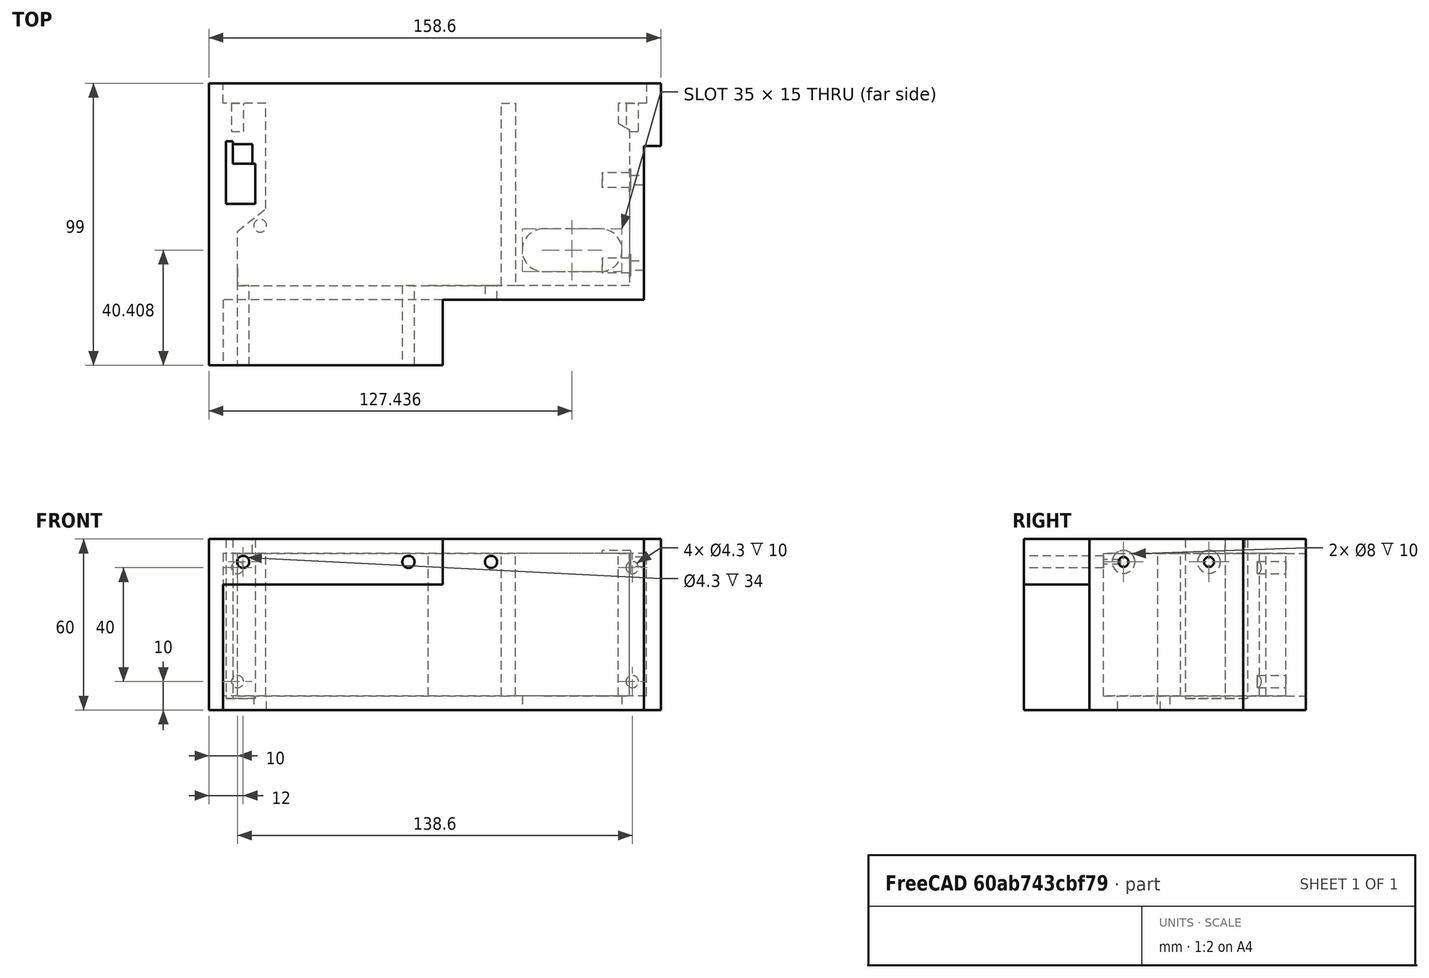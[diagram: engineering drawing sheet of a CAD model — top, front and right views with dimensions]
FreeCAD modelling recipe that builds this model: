
FCSTD DOCUMENT  (FreeCAD 0.21R33668 +7 (Git))
Label: speakerbox-L
License: All rights reserved
LicenseURL: http://en.wikipedia.org/wiki/All_rights_reserved
objects: Sketcher::SketchObject×10, PartDesign::Pocket×9, PartDesign::Plane×4, PartDesign::Pad×1, PartDesign::CoordinateSystem×1, PartDesign::Body×1, App::Part×1
note: 36 computed .brp shape members not serialized (recipe doc carries the construction recipe); baked Part::Feature solids carry a one-line shape summary decoded from their .brp
EXTERNAL_REF file=planB.FCStd obj=Spreadsheet

FEATURE [Sketcher::SketchObject] Sketch
  FullyConstrained = true
  MapMode = 5
  Support = -> [XY_Plane]
  expr: Constraints[13] = planB#<<data>>.central_h + planB#<<data>>.mungo_d + 2
  sketch-geometry (8):
    g0: LineSegment StartX=0 StartY=0 StartZ=0 EndX=82 EndY=0 EndZ=0
    g1: LineSegment StartX=158.6 StartY=99 StartZ=0 EndX=0 EndY=99 EndZ=0
    g2: LineSegment StartX=0 StartY=99 StartZ=0 EndX=0 EndY=0 EndZ=0
    g3: LineSegment StartX=82 StartY=0 StartZ=0 EndX=82 EndY=23 EndZ=0
    g4: LineSegment StartX=82 StartY=23 StartZ=0 EndX=152.6 EndY=23 EndZ=0
    g5: LineSegment StartX=152.6 StartY=23 StartZ=0 EndX=152.6 EndY=77 EndZ=0
    g6: LineSegment StartX=152.6 StartY=77 StartZ=0 EndX=158.6 EndY=77 EndZ=0
    g7: LineSegment StartX=158.6 StartY=77 StartZ=0 EndX=158.6 EndY=99 EndZ=0
  constraints (23):
    c: Coincident(g0,g3)
    c: Coincident(g7,g1)
    c: Coincident(g1,g2)
    c: Coincident(g2,g0)
    c: Horizontal(g0)
    c: Horizontal(g1)
    c: Vertical(g2)
    c: Coincident(g0,g-1)
    c: Coincident(g3,g4)
    c: Vertical(g3)
    c: Coincident(g4,g5)
    c: Horizontal(g4)
    c: Distance(g3) = 23
    c: Distance(g0) = 82
    c: DistanceX(g4) = 152.6
    c: Coincident(g5,g6)
    c: Vertical(g5)
    c: Coincident(g6,g7)
    c: Vertical(g7)
    c: Horizontal(g6)
    c: Distance(g6) = 6
    c: Distance(g5) = 54
    c: Distance(g7) = 22
FEATURE [PartDesign::Pad] Pad
  Direction = (0,0,1)
  Length = 60
  Length2 = 10
  Profile = -> Sketch
  ReferenceAxis = -> Sketch [N_Axis]
  Type = 0
  expr: Length = planB#<<data>>.speaker_w
FEATURE [PartDesign::Plane] DatumPlane
  AttachmentOffset = pos=(0,0,5) rot=(0,0,1;0rad)
  Length = 60
  MapMode = 2
  Placement = pos=(0,0,5) rot=(0,0,1;0rad)
  ResizeMode = 0
  Support = -> [XY_Plane]
  Width = 60
  expr: .AttachmentOffset.Base.z = planB#<<data>>.base_t
FEATURE [Sketcher::SketchObject] Sketch001
  FullyConstrained = false
  MapMode = 5
  Placement = pos=(0,0,5) rot=(0,0,1;0rad)
  Support = -> [DatumPlane]
  expr: Constraints[10] = planB#<<data>>.base_t * 2
  expr: Constraints[11] = planB#<<data>>.base_t
  sketch-geometry (21):
    g0: LineSegment StartX=5 StartY=129.209 StartZ=0 EndX=153.6 EndY=129.209 EndZ=0
    g1: LineSegment StartX=147.6 StartY=28 StartZ=0 EndX=77 EndY=28 EndZ=0
    g2: LineSegment StartX=77 StartY=28 StartZ=0 EndX=77 EndY=5 EndZ=0
    g3: LineSegment StartX=77 StartY=5 StartZ=0 EndX=10 EndY=5 EndZ=0
    g4: LineSegment StartX=153.6 StartY=129.209 StartZ=0 EndX=153.6 EndY=92 EndZ=0
    g5: LineSegment StartX=153.6 StartY=92 StartZ=0 EndX=143.6 EndY=92 EndZ=0
    g6: LineSegment StartX=5 StartY=92 StartZ=0 EndX=5 EndY=129.209 EndZ=0
    g7: LineSegment StartX=20 StartY=92 StartZ=0 EndX=5 EndY=92 EndZ=0
    g8: LineSegment StartX=10 StartY=47 StartZ=0 EndX=20 EndY=55 EndZ=0
    g9: LineSegment StartX=20 StartY=55 StartZ=0 EndX=20 EndY=92 EndZ=0
    g10: LineSegment StartX=147.6 StartY=82.6874 StartZ=0 EndX=147.6 EndY=28 EndZ=0
    g11: LineSegment StartX=143.6 StartY=92 StartZ=0 EndX=143.6 EndY=85 EndZ=0
    g12: LineSegment StartX=143.6 StartY=85 StartZ=0 EndX=147.6 EndY=82.6874 EndZ=0
    g13: LineSegment StartX=10 StartY=5 StartZ=0 EndX=10 EndY=28 EndZ=0
    g14: LineSegment StartX=10 StartY=28 StartZ=0 EndX=10 EndY=47 EndZ=0
    g15: LineSegment StartX=10 StartY=28 StartZ=0 EndX=102.6 EndY=28 EndZ=0
    g16: LineSegment StartX=102.6 StartY=28 StartZ=0 EndX=107.6 EndY=28 EndZ=0
    g17: LineSegment StartX=107.6 StartY=28 StartZ=0 EndX=77 EndY=28 EndZ=0
    g18: LineSegment StartX=102.6 StartY=28 StartZ=0 EndX=102.6 EndY=92 EndZ=0
    g19: LineSegment StartX=102.6 StartY=92 StartZ=0 EndX=107.6 EndY=92 EndZ=0
    g20: LineSegment StartX=107.6 StartY=92 StartZ=0 EndX=107.6 EndY=28 EndZ=0
  constraints (59):
    c: Coincident(g6,g0)
    c: Horizontal(g0)
    c: Coincident(g0,g4)
    c: Coincident(g10,g1)
    c: Horizontal(g1)
    c: Coincident(g1,g2)
    c: Vertical(g2)
    c: Coincident(g2,g3)
    c: Coincident(g3,g13)
    c: Horizontal(g3)
    c: DistanceX(g13) = 10
    c: DistanceY(g13) = 5
    c: DistanceX(g2) = 77
    c: DistanceX(g10) = 147.6
    c: Coincident(g4,g5)
    c: Vertical(g4)
    c: Coincident(g5,g11)
    c: Horizontal(g5)
    c: Distance(g2) = 23
    c: Coincident(g7,g6)
    c: Vertical(g6)
    c: Coincident(g9,g7)
    c: Coincident(g14,g8)
    c: Horizontal(g7)
    c: PointOnObject(g7,g5)
    c: Distance(g14,g7) = 45
    c: Coincident(g8,g9)
    c: Distance(g9) = 37
    c: Vertical(g9)
    c: Coincident(g12,g10)
    c: Vertical(g10)
    c: Distance(g12,g4) = 6
    c: Distance(g1,g5) = 64
    c: Distance(g5) = 10
    c: Coincident(g11,g12)
    c: Vertical(g11)
    c: Distance(g11) = 7
    c: Coincident(g13,g14)
    c: Vertical(g13)
    c: Vertical(g14)
    c: Coincident(g15,g13)
    c: Coincident(g17,g1)
    c: Coincident(g15,g16)
    c: Horizontal(g15)
    c: Coincident(g16,g17)
    c: Horizontal(g16)
    c: Horizontal(g17)
    c: Coincident(g15,g18)
    c: Vertical(g18)
    c: Coincident(g18,g19)
    c: Horizontal(g19)
    c: Coincident(g19,g20)
    c: Coincident(g20,g16)
    c: Vertical(g20)
    c: PointOnObject(g18,g7)
    c: Distance(g19) = 5
    c: Distance(g19,g10) = 40
    c: DistanceX(g-2,g6) = 5
    c: DistanceX(g7,g7) = 15
FEATURE [PartDesign::Pocket] Pocket  label="hollow out"
  BaseFeature = -> Pad
  Direction = (0,0,-1)
  Length = 50
  Length2 = 5
  Profile = -> Sketch001
  ReferenceAxis = -> Sketch001 [N_Axis]
  Reversed = true
  Type = 0
  expr: Length = planB#<<data>>.speaker_w - 2 * planB#<<data>>.base_t
FEATURE [PartDesign::CoordinateSystem] LCS_0
  AttacherType = Attacher::AttachEngine3D
  MapMode = 2
  Support = -> [X_Axis001]
FEATURE [PartDesign::Plane] DatumPlane001
  AttachmentOffset = pos=(0,0,60) rot=(0,0,1;0rad)
  Length = 60
  MapMode = 5
  Placement = pos=(0,0,60) rot=(0,0,1;0rad)
  ResizeMode = 0
  Support = -> [XY_Plane]
  Width = 60
  expr: .AttachmentOffset.Base.z = planB#<<data>>.speaker_w
FEATURE [Sketcher::SketchObject] Sketch002
  FullyConstrained = false
  MapMode = 5
  Support = -> [XY_Plane001]
  expr: Constraints[0] = planB#<<data>>.clearance_m4
  expr: Constraints[16] = planB#<<data>>.L_thickness + 0.4 * 2
  expr: Constraints[17] = planB#<<data>>.L_size + 0.4 * 2
  expr: Constraints[18] = planB#<<data>>.L_size - planB#<<data>>.L_thickness
  sketch-geometry (11):
    g0: Circle CenterX=18 CenterY=49 CenterZ=0 NormalX=0 NormalY=0 NormalZ=1 AngleXU=0 Radius=2.25
    g1: LineSegment StartX=6 StartY=78.6 StartZ=0 EndX=6 EndY=56.7 EndZ=0
    g2: LineSegment StartX=6 StartY=56.7 StartZ=0 EndX=16.3 EndY=56.7 EndZ=0
    g3: LineSegment StartX=16.3 StartY=56.7 StartZ=0 EndX=16.3 EndY=70.7 EndZ=0
    g4: LineSegment StartX=16.3 StartY=70.7 StartZ=0 EndX=8.4 EndY=70.7 EndZ=0
    g5: LineSegment StartX=8.4 StartY=70.7 StartZ=0 EndX=8.4 EndY=78.6 EndZ=0
    g6: LineSegment StartX=8.4 StartY=78.6 StartZ=0 EndX=6 EndY=78.6 EndZ=0
    g7: ArcOfCircle CenterX=117.436 CenterY=40.4082 CenterZ=0 NormalX=0 NormalY=0 NormalZ=1 AngleXU=0 Radius=7.5 StartAngle=1.5708 EndAngle=4.71239
    g8: ArcOfCircle CenterX=137.436 CenterY=40.4082 CenterZ=0 NormalX=0 NormalY=0 NormalZ=1 AngleXU=0 Radius=7.5 StartAngle=4.71239 EndAngle=7.85398
    g9: LineSegment StartX=117.436 StartY=32.9082 StartZ=0 EndX=137.436 EndY=32.9082 EndZ=0
    g10: LineSegment StartX=137.436 StartY=47.9082 StartZ=0 EndX=117.436 EndY=47.9082 EndZ=0
  constraints (29):
    c: Diameter(g0) = 4.5
    c: Vertical(g1)
    c: Coincident(g1,g2)
    c: Horizontal(g2)
    c: Coincident(g2,g3)
    c: Vertical(g3)
    c: Coincident(g3,g4)
    c: Horizontal(g4)
    c: Coincident(g4,g5)
    c: Vertical(g5)
    c: Coincident(g5,g6)
    c: Coincident(g6,g1)
    c: Horizontal(g6)
    c: DistanceX(g0) = 18
    c: DistanceY(g0) = 49
    c: DistanceX(g1) = 6
    c: Distance(g6) = 2.4
    c: Distance(g2) = 10.3
    c: Distance(g5) = 7.9
    c: Distance(g3) = 14
    c: DistanceY(g1) = 78.6
    c: Tangent(g7,g9) = -1.5708
    c: Tangent(g9,g8) = -1.5708
    c: Tangent(g8,g10) = -1.5708
    c: Tangent(g10,g7) = -1.5708
    c: Equal(g7,g8)
    c: Horizontal(g9)
    c: Distance(g9) = 20
    c: Distance(g7,g10) = 15
FEATURE [PartDesign::Pocket] Pocket001  label="threaded rod, power outlet"
  BaseFeature = -> Pocket
  Direction = (0,0,-1)
  Length = 30
  Length2 = 5
  Profile = -> Sketch002
  ReferenceAxis = -> Sketch002 [N_Axis]
  Reversed = true
  Type = 0
FEATURE [Sketcher::SketchObject] Sketch003
  FullyConstrained = false
  MapMode = 5
  Support = -> [XY_Plane001]
  sketch-geometry (4):
    g0: LineSegment StartX=5 StartY=0 StartZ=0 EndX=82.9999 EndY=0 EndZ=0
    g1: LineSegment StartX=82.9999 StartY=0 StartZ=0 EndX=82.9999 EndY=23 EndZ=0
    g2: LineSegment StartX=82.9999 StartY=23 StartZ=0 EndX=5 EndY=23 EndZ=0
    g3: LineSegment StartX=5 StartY=23 StartZ=0 EndX=5 EndY=0 EndZ=0
  constraints (11):
    c: Coincident(g0,g1)
    c: Coincident(g1,g2)
    c: Coincident(g2,g3)
    c: Coincident(g3,g0)
    c: Horizontal(g0)
    c: Horizontal(g2)
    c: Vertical(g1)
    c: Vertical(g3)
    c: Distance(g1) = 23
    c: PointOnObject(g0,g-1)
    c: DistanceX(g0) = 5
FEATURE [Sketcher::SketchObject] Sketch004
  FullyConstrained = true
  MapMode = 5
  Placement = pos=(0,0,0) rot=(1,0,0;1.5708rad)
  Support = -> [XZ_Plane]
  expr: Constraints[3] = planB#<<data>>.speaker_w - 8
  expr: Constraints[5] = planB#<<data>>.insert_diameter
  sketch-geometry (4):
    g0: Circle CenterX=12 CenterY=52 CenterZ=0 NormalX=0 NormalY=0 NormalZ=1 AngleXU=0 Radius=2.15
    g1: Circle CenterX=70 CenterY=52 CenterZ=0 NormalX=0 NormalY=0 NormalZ=1 AngleXU=0 Radius=2.15
    g2: LineSegment StartX=12 StartY=52 StartZ=0 EndX=70 EndY=52 EndZ=0
    g3: Circle CenterX=99 CenterY=52 CenterZ=0 NormalX=0 NormalY=0 NormalZ=1 AngleXU=0 Radius=2.15
  constraints (11):
    c: Coincident(g2,g0)
    c: Coincident(g2,g1)
    c: Horizontal(g2)
    c: DistanceY(g-1,g0) = 52
    c: Equal(g0,g1)
    c: Diameter(g1) = 4.3
    c: DistanceX(g0) = 12
    c: DistanceX(g1) = 70
    c: PointOnObject(g3,g2)
    c: Equal(g1,g3)
    c: DistanceX(g3) = 99
FEATURE [PartDesign::Plane] DatumPlane002
  AttachmentOffset = pos=(0,0,138) rot=(0,0,1;0rad)
  Length = 60
  MapMode = 5
  Placement = pos=(138,-3.06e-14,3.06e-14) rot=(0.57735,0.57735,0.57735;2.0944rad)
  ResizeMode = 0
  Support = -> [YZ_Plane]
  Width = 60
FEATURE [Sketcher::SketchObject] Sketch005
  FullyConstrained = true
  MapMode = 5
  Placement = pos=(138,-3.06e-14,3.06e-14) rot=(0.57735,0.57735,0.57735;2.0944rad)
  Support = -> [DatumPlane002]
  expr: Constraints[1] = planB#<<data>>.clearance_m3
  expr: Constraints[5] = planB#<<data>>.speaker_w - 8
  sketch-geometry (3):
    g0: Circle CenterX=35 CenterY=52 CenterZ=0 NormalX=0 NormalY=0 NormalZ=1 AngleXU=0 Radius=1.75
    g1: Circle CenterX=65 CenterY=52 CenterZ=0 NormalX=0 NormalY=0 NormalZ=1 AngleXU=0 Radius=1.75
    g2: LineSegment StartX=35 StartY=52 StartZ=0 EndX=65 EndY=52 EndZ=0
  constraints (8):
    c: Equal(g1,g0)
    c: Diameter(g1) = 3.5
    c: Coincident(g2,g0)
    c: Coincident(g2,g1)
    c: Horizontal(g2)
    c: DistanceY(g-1,g0) = 52
    c: DistanceX(g0) = 35
    c: DistanceX(g1) = 65
FEATURE [Sketcher::SketchObject] Sketch006
  FullyConstrained = true
  MapMode = 5
  Placement = pos=(138,-3.06e-14,3.06e-14) rot=(0.57735,0.57735,0.57735;2.0944rad)
  Support = -> [DatumPlane002]
  expr: Constraints[5] = planB#<<data>>.speaker_w - 8
  sketch-geometry (3):
    g0: Circle CenterX=35 CenterY=52 CenterZ=0 NormalX=0 NormalY=0 NormalZ=1 AngleXU=0 Radius=4
    g1: Circle CenterX=65 CenterY=52 CenterZ=0 NormalX=0 NormalY=0 NormalZ=1 AngleXU=0 Radius=4
    g2: LineSegment StartX=35 StartY=52 StartZ=0 EndX=65 EndY=52 EndZ=0
  constraints (8):
    c: Equal(g1,g0)
    c: Diameter(g1) = 8
    c: Coincident(g2,g0)
    c: Coincident(g2,g1)
    c: Horizontal(g2)
    c: DistanceY(g-1,g0) = 52
    c: DistanceX(g0) = 35
    c: DistanceX(g1) = 65
FEATURE [Sketcher::SketchObject] Sketch009
  FullyConstrained = true
  MapMode = 5
  Placement = pos=(0,0,60) rot=(0,0,1;0rad)
  Support = -> [DatumPlane001]
  expr: Constraints[13] = planB#<<data>>.L_thickness + 0.4 * 2
  expr: Constraints[14] = planB#<<data>>.L_size + 0.4 * 2
  expr: Constraints[15] = planB#<<data>>.L_size - planB#<<data>>.L_thickness
  sketch-geometry (6):
    g0: LineSegment StartX=6 StartY=78.6 StartZ=0 EndX=6 EndY=56.7 EndZ=0
    g1: LineSegment StartX=6 StartY=56.7 StartZ=0 EndX=16.3 EndY=56.7 EndZ=0
    g2: LineSegment StartX=16.3 StartY=56.7 StartZ=0 EndX=16.3 EndY=70.7 EndZ=0
    g3: LineSegment StartX=16.3 StartY=70.7 StartZ=0 EndX=8.4 EndY=70.7 EndZ=0
    g4: LineSegment StartX=8.4 StartY=70.7 StartZ=0 EndX=8.4 EndY=78.6 EndZ=0
    g5: LineSegment StartX=8.4 StartY=78.6 StartZ=0 EndX=6 EndY=78.6 EndZ=0
  constraints (18):
    c: Vertical(g0)
    c: Coincident(g0,g1)
    c: Horizontal(g1)
    c: Coincident(g1,g2)
    c: Vertical(g2)
    c: Coincident(g2,g3)
    c: Horizontal(g3)
    c: Coincident(g3,g4)
    c: Vertical(g4)
    c: Coincident(g4,g5)
    c: Coincident(g5,g0)
    c: Horizontal(g5)
    c: DistanceX(g0) = 6
    c: Distance(g5) = 2.4
    c: Distance(g1) = 10.3
    c: Distance(g4) = 7.9
    c: Distance(g2) = 14
    c: DistanceY(g0) = 78.6
FEATURE [PartDesign::Pocket] Pocket008  label="L hole"
  BaseFeature = -> Pocket001
  Direction = (0,0,-1)
  Length = 56
  Length2 = 5
  Profile = -> Sketch009
  ReferenceAxis = -> Sketch009 [N_Axis]
  Type = 0
FEATURE [PartDesign::Pocket] Pocket002  label="hollow for psu"
  BaseFeature = -> Pocket008
  Direction = (0,0,-1)
  Length = 44
  Length2 = 5
  Profile = -> Sketch003
  ReferenceAxis = -> Sketch003 [N_Axis]
  Reversed = true
  Type = 0
  expr: Length = planB#<<data>>.speaker_w - 16
FEATURE [PartDesign::Pocket] Pocket003  label="bottom screwholes"
  BaseFeature = -> Pocket002
  Direction = (0,1,2e-16)
  Length = 34
  Length2 = 5
  Profile = -> Sketch004
  ReferenceAxis = -> Sketch004 [N_Axis]
  Type = 0
FEATURE [PartDesign::Pocket] Pocket004  label="side screwholes"
  BaseFeature = -> Pocket003
  Direction = (-1,1e-16,-1e-16)
  Length = 9
  Length2 = 5
  Profile = -> Sketch005
  ReferenceAxis = -> Sketch005 [N_Axis]
  Reversed = true
  Type = 1
FEATURE [PartDesign::Pocket] Pocket005  label="side screwhole clearance"
  BaseFeature = -> Pocket004
  Direction = (-1,1e-16,-1e-16)
  Length = 10
  Length2 = 5
  Profile = -> Sketch006
  ReferenceAxis = -> Sketch006 [N_Axis]
  Reversed = true
  Type = 0
FEATURE [Sketcher::SketchObject] Sketch010
  FullyConstrained = true
  MapMode = 5
  Placement = pos=(0,0,60) rot=(0,0,1;0rad)
  Support = -> [DatumPlane001]
  sketch-geometry (4):
    g0: LineSegment StartX=7 StartY=77.6 StartZ=0 EndX=15.3 EndY=77.6 EndZ=0
    g1: LineSegment StartX=15.3 StartY=77.6 StartZ=0 EndX=15.3 EndY=57.7 EndZ=0
    g2: LineSegment StartX=15.3 StartY=57.7 StartZ=0 EndX=7 EndY=57.7 EndZ=0
    g3: LineSegment StartX=7 StartY=57.7 StartZ=0 EndX=7 EndY=77.6 EndZ=0
  constraints (12):
    c: Coincident(g0,g1)
    c: Coincident(g1,g2)
    c: Coincident(g2,g3)
    c: Coincident(g3,g0)
    c: Horizontal(g0)
    c: Horizontal(g2)
    c: Vertical(g1)
    c: Vertical(g3)
    c: DistanceX(g0) = 7
    c: DistanceY(g0) = 77.6
    c: DistanceX(g1) = 15.3
    c: DistanceY(g1) = 57.7
FEATURE [PartDesign::Pocket] Pocket009
  BaseFeature = -> Pocket005
  Direction = (0,0,-1)
  Length = 5
  Length2 = 5
  Profile = -> Sketch010
  ReferenceAxis = -> Sketch010 [N_Axis]
  Type = 0
FEATURE [PartDesign::Plane] DatumPlane003
  AttachmentOffset = pos=(0,0,100) rot=(0,0,1;0rad)
  Length = 60
  MapMode = 5
  Placement = pos=(0,100,2.22e-14) rot=(0,0.707107,0.707107;3.14159rad)
  ResizeMode = 0
  Support = -> [XZ_Plane]
  Width = 60
FEATURE [Sketcher::SketchObject] Sketch011
  FullyConstrained = true
  MapMode = 5
  Placement = pos=(0,100,2.22e-14) rot=(0,0.707107,0.707107;3.14159rad)
  Support = -> [DatumPlane003]
  expr: Constraints[15] = planB#<<data>>.insert_diameter
  sketch-geometry (8):
    g0: Circle CenterX=-148.6 CenterY=50 CenterZ=0 NormalX=0 NormalY=0 NormalZ=1 AngleXU=0 Radius=2.15
    g1: LineSegment StartX=-148.6 StartY=50 StartZ=0 EndX=-10 EndY=50 EndZ=0
    g2: LineSegment StartX=-10 StartY=50 StartZ=0 EndX=-10 EndY=10 EndZ=0
    g3: LineSegment StartX=-10 StartY=10 StartZ=0 EndX=-148.6 EndY=10 EndZ=0
    g4: LineSegment StartX=-148.6 StartY=10 StartZ=0 EndX=-148.6 EndY=50 EndZ=0
    g5: Circle CenterX=-148.6 CenterY=10 CenterZ=0 NormalX=0 NormalY=0 NormalZ=1 AngleXU=0 Radius=2.15
    g6: Circle CenterX=-10 CenterY=10 CenterZ=0 NormalX=0 NormalY=0 NormalZ=1 AngleXU=0 Radius=2.15
    g7: Circle CenterX=-10 CenterY=50 CenterZ=0 NormalX=0 NormalY=0 NormalZ=1 AngleXU=0 Radius=2.15
  constraints (20):
    c: Coincident(g1,g2)
    c: Coincident(g2,g3)
    c: Coincident(g3,g4)
    c: Coincident(g4,g1)
    c: Horizontal(g1)
    c: Horizontal(g3)
    c: Vertical(g2)
    c: Vertical(g4)
    c: Coincident(g1,g0)
    c: Coincident(g5,g3)
    c: Coincident(g6,g2)
    c: Coincident(g7,g1)
    c: Equal(g0,g7)
    c: Equal(g7,g6)
    c: Equal(g6,g5)
    c: Diameter(g6) = 4.3
    c: DistanceY(g5) = 10
    c: DistanceX(g6) = -10
    c: DistanceY(g4,g4) = 40
    c: DistanceX(g5) = -148.6
FEATURE [PartDesign::Pocket] Pocket010
  BaseFeature = -> Pocket009
  Direction = (0,-1,-2e-16)
  Length = 18
  Length2 = 5
  Profile = -> Sketch011
  ReferenceAxis = -> Sketch011 [N_Axis]
  Type = 0
FEATURE [PartDesign::Body] Body
  Group = -> [Sketch,Pad,DatumPlane,Sketch001,Pocket,DatumPlane001,Sketch002,Pocket001,Pocket008,Sketch003,Pocket002,Sketch004,Pocket003,DatumPlane002,Sketch005,Pocket004,Sketch006,Pocket005,Sketch009,Sketch010,Pocket009,DatumPlane003,Sketch011,Pocket010]
  Origin = -> Origin
  Tip = -> Pocket010
FEATURE [App::Part] speakerbox  label="speakerbox-L"
  Group = -> [LCS_0,Body]
  Origin = -> Origin001
